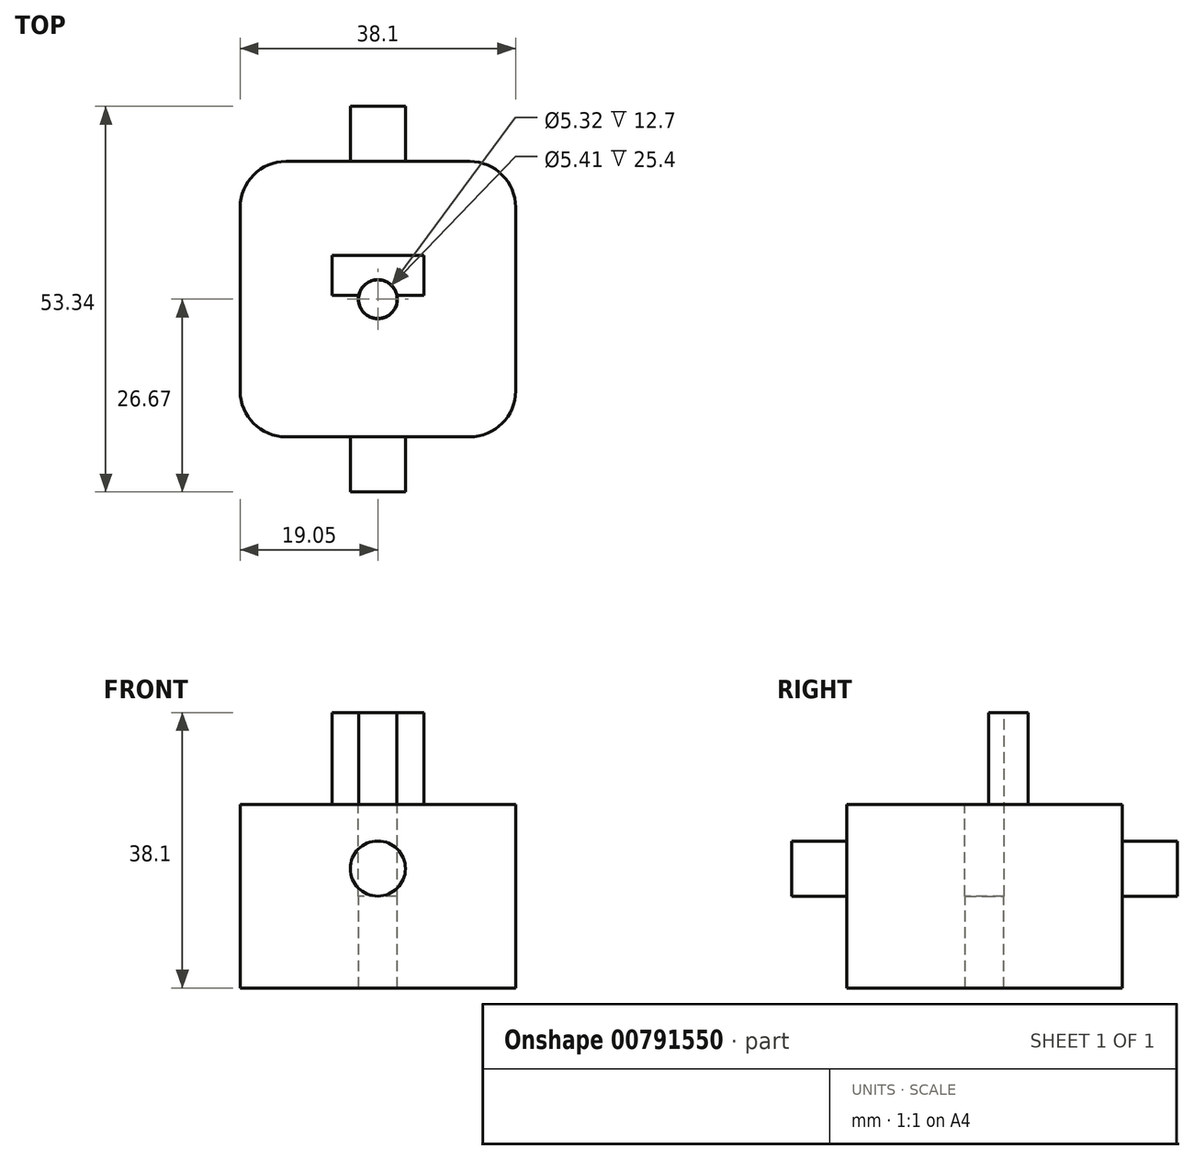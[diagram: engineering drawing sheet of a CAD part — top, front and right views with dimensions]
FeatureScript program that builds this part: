
annotation { "Feature Type Name" : "Feature", "Feature Type Description" : "" }
export const myFeature = defineFeature(function(context is Context, id is Id, definition is map)
    precondition{}
    {
        {
            var Q0;
            Q0=qCreatedBy(makeId("Top.planeOp"),FACE);
            var sketch = newSketch(context, id + "F0", { "sketchPlane" : qUnion([Q0])});
            skLineSegment(sketch, "E0.bottom", {"start": v(6.35, 0) * mm, "end": v(31.75, 0) * mm});
            skLineSegment(sketch, "E0.top", {"start": v(6.35, 38.1) * mm, "end": v(31.75, 38.1) * mm});
            skLineSegment(sketch, "E0.left", {"start": v(0, 6.35) * mm, "end": v(0, 31.75) * mm});
            skLineSegment(sketch, "E0.right", {"start": v(38.1, 6.35) * mm, "end": v(38.1, 31.75) * mm});
            skPoint(sketch, "E1.visualSharp", {"position": v(0, 0) * mm});
            skArc(sketch, "E1.filletArc", {"start": v(0, 6.35) * mm, "mid": v(1.86, 1.86) * mm, "end": v(6.35, 0) * mm});
            skPoint(sketch, "E2.visualSharp", {"position": v(0, 38.1) * mm});
            skArc(sketch, "E2.filletArc", {"start": v(6.35, 38.1) * mm, "mid": v(1.86, 36.24) * mm, "end": v(0, 31.75) * mm});
            skPoint(sketch, "E3.visualSharp", {"position": v(38.1, 38.1) * mm});
            skArc(sketch, "E3.filletArc", {"start": v(38.1, 31.75) * mm, "mid": v(36.24, 36.24) * mm, "end": v(31.75, 38.1) * mm});
            skPoint(sketch, "E4.visualSharp", {"position": v(38.1, 0) * mm});
            skArc(sketch, "E4.filletArc", {"start": v(31.75, 0) * mm, "mid": v(36.24, 1.86) * mm, "end": v(38.1, 6.35) * mm});
            skSolve(sketch);
        }
        {
            var Q0;
            Q0=makeQuery(id+"F0.imprint","IMPRINT",FACE,{"disambiguationData":[TD([[makeQuery(id+"F0.imprint","IMPRINT",EDGE,{"derivedFrom":sQuery(id+"F0.wireOp",EDGE,"E0.bottom")}),1.0]])]});
            extrude(context, id + "F1", {"entities" : qUnion([Q0]), "depth" : 25.4 * mm, "offsetDistance" : 25.4 * mm});
        }
        {
            var Q0;
            Q0=makeQuery(id+"F1.opExtrude","CAP_FACE",FACE,{"disambiguationData":[OSD([sQuery(id+"F0.wireOp",EDGE,"E0.bottom"),sQuery(id+"F0.wireOp",EDGE,"E0.top"),sQuery(id+"F0.wireOp",EDGE,"E0.left"),sQuery(id+"F0.wireOp",EDGE,"E0.right")])],"isStart":false});
            var sketch = newSketch(context, id + "F2", { "sketchPlane" : qUnion([Q0])});
            skSolve(sketch);
        }
        {
            var Q0;
            Q0=makeQuery(id+"F2.imprint","IMPRINT",FACE,{"disambiguationData":[TD([[makeQuery(id+"F2.imprint","IMPRINT",EDGE,{"derivedFrom":makeQuery(id+"F1.opExtrude","CAP_EDGE",EDGE,{"disambiguationData":[OSD([sQuery(id+"F0.wireOp",EDGE,"E0.bottom")])],"isStart":false})}),1.0]])]});
            var sketch = newSketch(context, id + "F3", { "sketchPlane" : qUnion([Q0])});
            skCircle(sketch, "E5", {"center": v(19.05, 19.05) * mm, "radius": 2.66 * mm});
            skSolve(sketch);
        }
        {
            var Q0;
            Q0=makeQuery(id+"F2.imprint","IMPRINT",FACE,{"disambiguationData":[TD([[makeQuery(id+"F2.imprint","IMPRINT",EDGE,{"derivedFrom":makeQuery(id+"F1.opExtrude","CAP_EDGE",EDGE,{"disambiguationData":[OSD([sQuery(id+"F0.wireOp",EDGE,"E0.bottom")])],"isStart":false})}),1.0]])]});
            var sketch = newSketch(context, id + "F4", { "sketchPlane" : qUnion([Q0])});
            skLineSegment(sketch, "E6.bottom", {"start": v(25.4, 19.6) * mm, "end": v(12.7, 19.6) * mm});
            skLineSegment(sketch, "E6.top", {"start": v(25.4, 25.07) * mm, "end": v(12.7, 25.07) * mm});
            skLineSegment(sketch, "E6.left", {"start": v(25.4, 19.6) * mm, "end": v(25.4, 25.07) * mm});
            skLineSegment(sketch, "E6.right", {"start": v(12.7, 19.6) * mm, "end": v(12.7, 25.07) * mm});
            skSolve(sketch);
        }
        {
            var Q0;
            Q0 = qSketchRegion(id + "F4", true);
            extrude(context, id + "F5", {"entities" : qUnion([Q0]), "operationType" : NewBodyOperationType.ADD, "depth" : 12.7 * mm, "offsetDistance" : 25.4 * mm});
        }
        {
            var Q0;
            Q0 = qSketchRegion(id + "F3", true);
            extrude(context, id + "F6", {"entities" : qUnion([Q0]), "operationType" : NewBodyOperationType.REMOVE, "oppositeDirection" : true, "depth" : 25.4 * mm, "offsetDistance" : 25.4 * mm});
        }
        {
            var Q0;
            Q0=makeQuery(id+"F5.opExtrude","CAP_FACE",FACE,{"disambiguationData":[OSD([sQuery(id+"F4.wireOp",EDGE,"E6.bottom"),sQuery(id+"F4.wireOp",EDGE,"E6.top"),sQuery(id+"F4.wireOp",EDGE,"E6.left"),sQuery(id+"F4.wireOp",EDGE,"E6.right")])],"isStart":false});
            var sketch = newSketch(context, id + "F7", { "sketchPlane" : qUnion([Q0])});
            skCircle(sketch, "E7", {"center": v(19.05, 19.05) * mm, "radius": 2.7 * mm});
            skPoint(sketch, "E7.centerSnap0", {"position": v(19.05, 19.6) * mm});
            skSolve(sketch);
        }
        {
            var Q0;
            Q0 = qSketchRegion(id + "F7", true);
            extrude(context, id + "F8", {"entities" : qUnion([Q0]), "operationType" : NewBodyOperationType.REMOVE, "oppositeDirection" : true, "depth" : 25.4 * mm, "offsetDistance" : 25.4 * mm});
        }
        {
            var Q0;
            Q0=makeQuery(id+"F1.opExtrude","SWEPT_FACE",FACE,{"disambiguationData":[OSD([sQuery(id+"F0.wireOp",EDGE,"E0.bottom")])]});
            var sketch = newSketch(context, id + "F9", { "sketchPlane" : qUnion([Q0])});
            skCircle(sketch, "E8", {"center": v(19.05, 16.51) * mm, "radius": 3.81 * mm});
            skPoint(sketch, "E8.centerSnap0", {"position": v(19.05, 25.4) * mm});
            skSolve(sketch);
        }
        {
            var Q0;
            Q0=makeQuery(id+"F1.opExtrude","SWEPT_FACE",FACE,{"disambiguationData":[OSD([sQuery(id+"F0.wireOp",EDGE,"E0.top")])]});
            var sketch = newSketch(context, id + "F10", { "sketchPlane" : qUnion([Q0])});
            skCircle(sketch, "E9", {"center": v(-19.05, 16.51) * mm, "radius": 3.81 * mm});
            skSolve(sketch);
        }
        {
            var Q0;
            Q0=makeQuery(id+"F9.imprint","IMPRINT",FACE,{"disambiguationData":[TD([[makeQuery(id+"F9.imprint","IMPRINT",EDGE,{"derivedFrom":sQuery(id+"F9.wireOp",EDGE,"E8")}),1.0]])]});
            extrude(context, id + "F11", {"entities" : qUnion([Q0]), "operationType" : NewBodyOperationType.ADD, "depth" : 7.62 * mm, "offsetDistance" : 25.4 * mm});
        }
        {
            var Q0;
            Q0=makeQuery(id+"F10.imprint","IMPRINT",FACE,{"disambiguationData":[TD([[makeQuery(id+"F10.imprint","IMPRINT",EDGE,{"derivedFrom":sQuery(id+"F10.wireOp",EDGE,"E9")}),1.0]])]});
            extrude(context, id + "F12", {"entities" : qUnion([Q0]), "operationType" : NewBodyOperationType.ADD, "depth" : 7.62 * mm, "offsetDistance" : 25.4 * mm});
        }
    });
